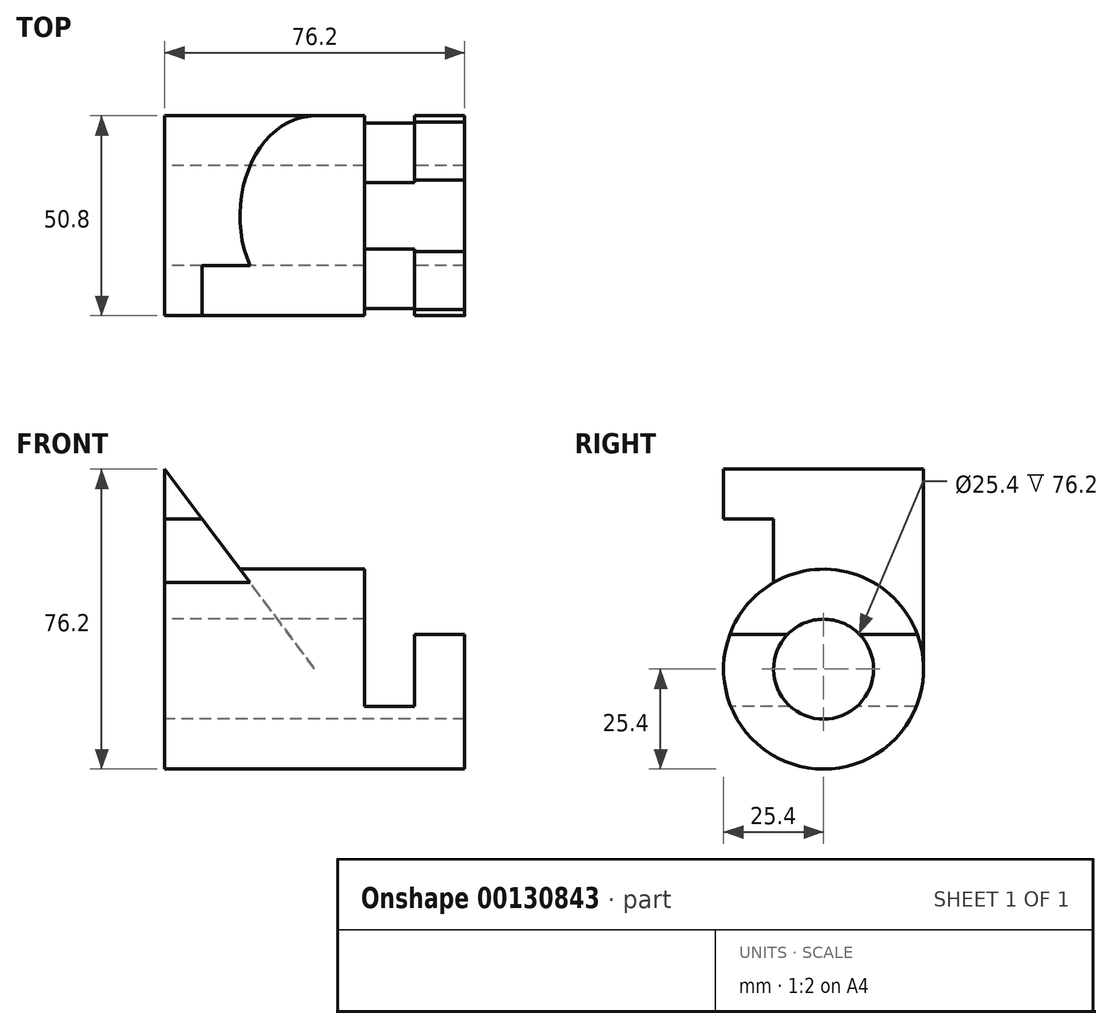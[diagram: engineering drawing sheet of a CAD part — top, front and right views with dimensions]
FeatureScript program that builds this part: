
annotation { "Feature Type Name" : "Feature", "Feature Type Description" : "" }
export const myFeature = defineFeature(function(context is Context, id is Id, definition is map)
    precondition{}
    {
        {
            var Q0;
            Q0=qCreatedBy(makeId("Right.planeOp"),FACE);
            var sketch = newSketch(context, id + "F0", { "sketchPlane" : qUnion([Q0])});
            skCircle(sketch, "E0", {"center": v(0, 0) * mm, "radius": 12.7 * mm});
            skCircle(sketch, "E1", {"center": v(0, 0) * mm, "radius": 25.4 * mm});
            skSolve(sketch);
        }
        {
            var Q0;
            Q0 = qSketchRegion(id + "F0", true);
            extrude(context, id + "F1", {"entities" : qUnion([Q0]), "depth" : 76.2 * mm});
        }
        {
            var Q0;
            Q0=qCreatedBy(makeId("Front.planeOp"),FACE);
            var sketch = newSketch(context, id + "F2", { "sketchPlane" : qUnion([Q0])});
            skLineSegment(sketch, "E2.0", {"start": v(76.2, 25.4) * mm, "end": v(76.2, -25.4) * mm});
            skLineSegment(sketch, "E3", {"start": v(76.2, 8.84) * mm, "end": v(63.5, 8.84) * mm});
            skLineSegment(sketch, "E4", {"start": v(63.5, 8.84) * mm, "end": v(63.5, -9.53) * mm});
            skLineSegment(sketch, "E5", {"start": v(63.5, -9.53) * mm, "end": v(50.8, -9.53) * mm});
            skLineSegment(sketch, "E6", {"start": v(50.8, -9.53) * mm, "end": v(50.8, 25.4) * mm});
            skLineSegment(sketch, "E7", {"start": v(50.8, 25.4) * mm, "end": v(76.2, 25.4) * mm});
            skSolve(sketch);
        }
        {
            var Q0;
            {var subQ0=sQuery(id+"F2.wireOp",EDGE,"E3");Q0=makeQuery(id+"F2.imprint","IMPRINT",FACE,{"disambiguationData":[TD([[makeQuery(id+"F2.imprint","IMPRINT",EDGE,{"derivedFrom":subQ0}),-1.0]])]});}
            extrude(context, id + "F3", {"entities" : qUnion([Q0]), "operationType" : NewBodyOperationType.REMOVE, "endBound" : BoundingType.SYMMETRIC, "oppositeDirection" : true, "depth" : 50.8 * mm});
        }
        {
            var Q0;
            Q0=qCreatedBy(makeId("Front.planeOp"),FACE);
            var sketch = newSketch(context, id + "F4", { "sketchPlane" : qUnion([Q0])});
            skLineSegment(sketch, "E8", {"start": v(0, 0) * mm, "end": v(0, 50.8) * mm});
            skLineSegment(sketch, "E9", {"start": v(0, 50.8) * mm, "end": v(38.1, 0) * mm});
            skLineSegment(sketch, "E10", {"start": v(38.1, 0) * mm, "end": v(0, 0) * mm});
            skSolve(sketch);
        }
        {
            var Q0;
            Q0=makeQuery(id+"F4.imprint","IMPRINT",FACE,{"disambiguationData":[TD([[makeQuery(id+"F4.imprint","IMPRINT",EDGE,{"derivedFrom":sQuery(id+"F4.wireOp",EDGE,"E8")}),-1.0]])]});
            extrude(context, id + "F5", {"entities" : qUnion([Q0]), "operationType" : NewBodyOperationType.ADD, "endBound" : BoundingType.SYMMETRIC, "depth" : 50.8 * mm});
        }
        {
            var Q0;
            Q0=makeQuery(id+"F5.boolean.opBoolean","MERGE",FACE,{"derivedFrom":[makeQuery(id+"F1.opExtrude","CAP_FACE",FACE,{"disambiguationData":[OSD([sQuery(id+"F0.wireOp",EDGE,"E0"),sQuery(id+"F0.wireOp",EDGE,"E1")])],"isStart":true}),makeQuery(id+"F5.opExtrude","SWEPT_FACE",FACE,{"disambiguationData":[OSD([sQuery(id+"F4.wireOp",EDGE,"E8")])]})]});
            var sketch = newSketch(context, id + "F6", { "sketchPlane" : qUnion([Q0])});
            skCircle(sketch, "E11", {"center": v(0, 0) * mm, "radius": 12.7 * mm});
            skLineSegment(sketch, "E12.0", {"start": v(-25.4, 0) * mm, "end": v(-25.4, 50.8) * mm});
            skLineSegment(sketch, "E13.0", {"start": v(25.4, 50.8) * mm, "end": v(-25.4, 50.8) * mm});
            skLineSegment(sketch, "E14.bottom", {"start": v(-12.7, 50.8) * mm, "end": v(25.4, 50.8) * mm});
            skLineSegment(sketch, "E14.top", {"start": v(-12.7, 38.1) * mm, "end": v(25.4, 38.1) * mm});
            skLineSegment(sketch, "E14.left", {"start": v(-12.7, 50.8) * mm, "end": v(-12.7, 38.1) * mm});
            skLineSegment(sketch, "E14.right", {"start": v(25.4, 50.8) * mm, "end": v(25.4, 38.1) * mm});
            skCircle(sketch, "E15.0", {"center": v(0, 0) * mm, "radius": 25.4 * mm});
            skLineSegment(sketch, "E16", {"start": v(25.4, 38.1) * mm, "end": v(25.4, 0) * mm});
            skLineSegment(sketch, "E17", {"start": v(12.7, 38.1) * mm, "end": v(12.7, 22) * mm});
            skSolve(sketch);
        }
        {
            var Q0;
            Q0=makeQuery(id+"F6.imprint","IMPRINT",FACE,{"disambiguationData":[TD([[makeQuery(id+"F6.imprint","IMPRINT",EDGE,{"disambiguationData":[OD(0.0)],"derivedFrom":sQuery(id+"F6.wireOp",EDGE,"E11")}),1.0]])]});
            extrude(context, id + "F7", {"entities" : qUnion([Q0]), "operationType" : NewBodyOperationType.REMOVE, "endBound" : BoundingType.THROUGH_ALL, "oppositeDirection" : true, "depth" : 25.4 * mm});
        }
        {
            var Q0;
            Q0=makeQuery(id+"F6.imprint","IMPRINT",FACE,{"disambiguationData":[TD([[makeQuery(id+"F6.imprint","IMPRINT",EDGE,{"derivedFrom":sQuery(id+"F6.wireOp",EDGE,"E14.bottom")}),1.0]])]});
            var Q1;
            {var subQ0=sQuery(id+"F6.wireOp",EDGE,"E16");Q1=makeQuery(id+"F6.imprint","IMPRINT",FACE,{"disambiguationData":[TD([[makeQuery(id+"F6.imprint","IMPRINT",EDGE,{"derivedFrom":subQ0}),1.0]])]});}
            extrude(context, id + "F8", {"entities" : qUnion([Q0, Q1]), "operationType" : NewBodyOperationType.REMOVE, "endBound" : BoundingType.THROUGH_ALL, "oppositeDirection" : true, "depth" : 25.4 * mm});
        }
    });
